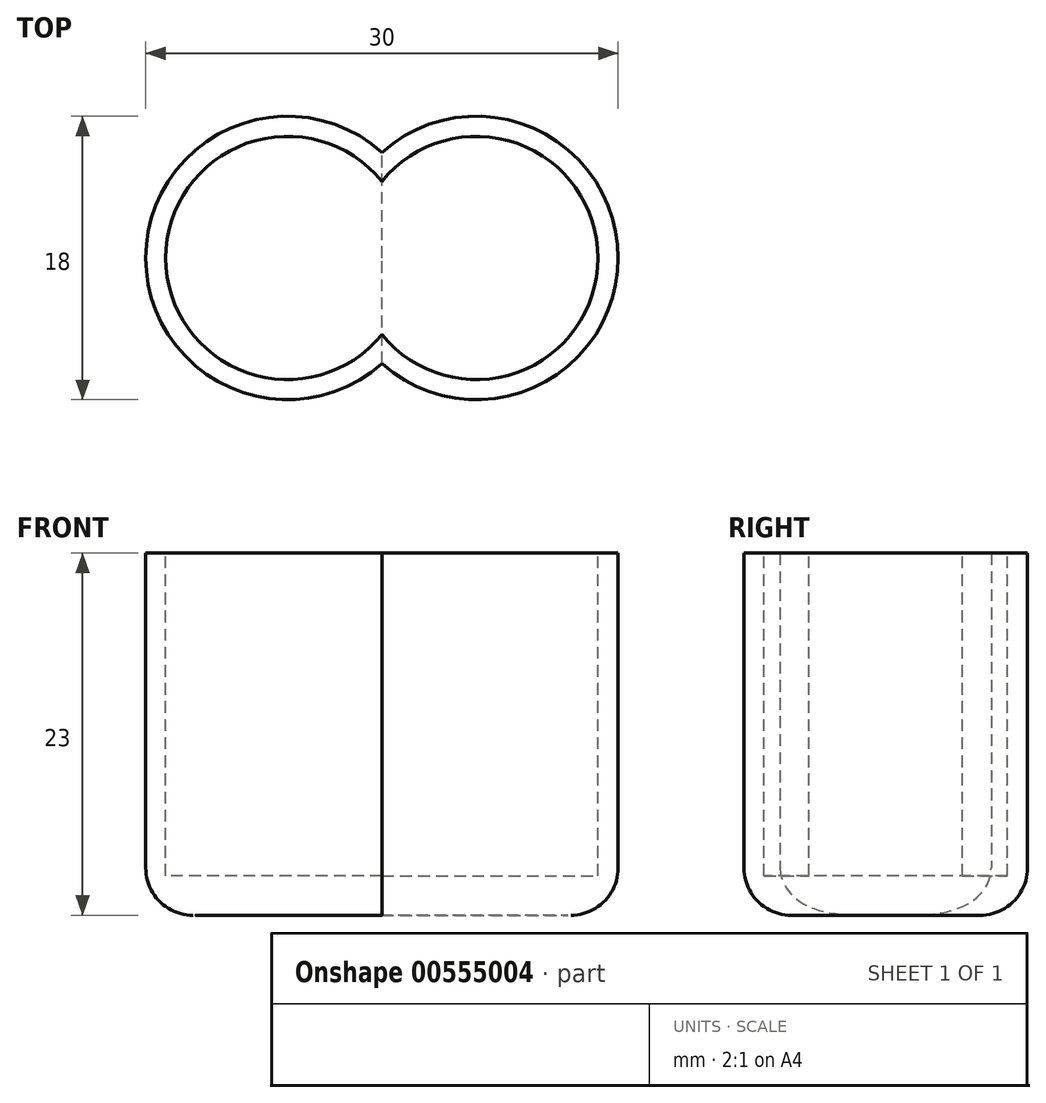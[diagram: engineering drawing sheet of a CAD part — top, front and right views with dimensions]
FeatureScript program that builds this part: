
annotation { "Feature Type Name" : "Feature", "Feature Type Description" : "" }
export const myFeature = defineFeature(function(context is Context, id is Id, definition is map)
    precondition{}
    {
        {
            var Q0;
            Q0=qCreatedBy(makeId("Top.planeOp"),FACE);
            var sketch = newSketch(context, id + "F0", { "sketchPlane" : qUnion([Q0])});
            skCircle(sketch, "E0", {"center": v(6, 0) * mm, "radius": 9 * mm});
            skCircle(sketch, "E1", {"center": v(-6, 0) * mm, "radius": 9 * mm});
            skSolve(sketch);
        }
        {
            var Q0;
            Q0 = qSketchRegion(id + "F0", true);
            extrude(context, id + "F1", {"entities" : qUnion([Q0]), "depth" : 23 * mm, "offsetDistance" : 25 * mm});
        }
        {
            var Q0;
            Q0=makeQuery(id+"F1.opExtrude","CAP_FACE",FACE,{"disambiguationData":[OSD([sQuery(id+"F0.wireOp",EDGE,"E0"),sQuery(id+"F0.wireOp",EDGE,"E1")])],"isStart":false});
            var sketch = newSketch(context, id + "F2", { "sketchPlane" : qUnion([Q0])});
            skCircle(sketch, "E2", {"center": v(6, 0) * mm, "radius": 7.73 * mm});
            skCircle(sketch, "E3", {"center": v(-6, 0) * mm, "radius": 7.73 * mm});
            skSolve(sketch);
        }
        {
            var Q0;
            Q0 = qSketchRegion(id + "F2", true);
            extrude(context, id + "F3", {"entities" : qUnion([Q0]), "operationType" : NewBodyOperationType.REMOVE, "oppositeDirection" : true, "depth" : 20.5 * mm, "offsetDistance" : 25 * mm});
        }
        {
            var Q0;
            Q0=makeQuery(id+"F1.opExtrude","CAP_EDGE",EDGE,{"disambiguationData":[OSD([sQuery(id+"F0.wireOp",EDGE,"E0")])],"isStart":true});
            var Q1;
            Q1=makeQuery(id+"F1.opExtrude","CAP_EDGE",EDGE,{"disambiguationData":[OSD([sQuery(id+"F0.wireOp",EDGE,"E1")])],"isStart":true});
            fillet(context, id + "F4", {"entities" : qUnion([Q0, Q1]), "radius" : 3 * mm, "tangentPropagation" : true, "allowEdgeOverflow" : false});
        }
    });
